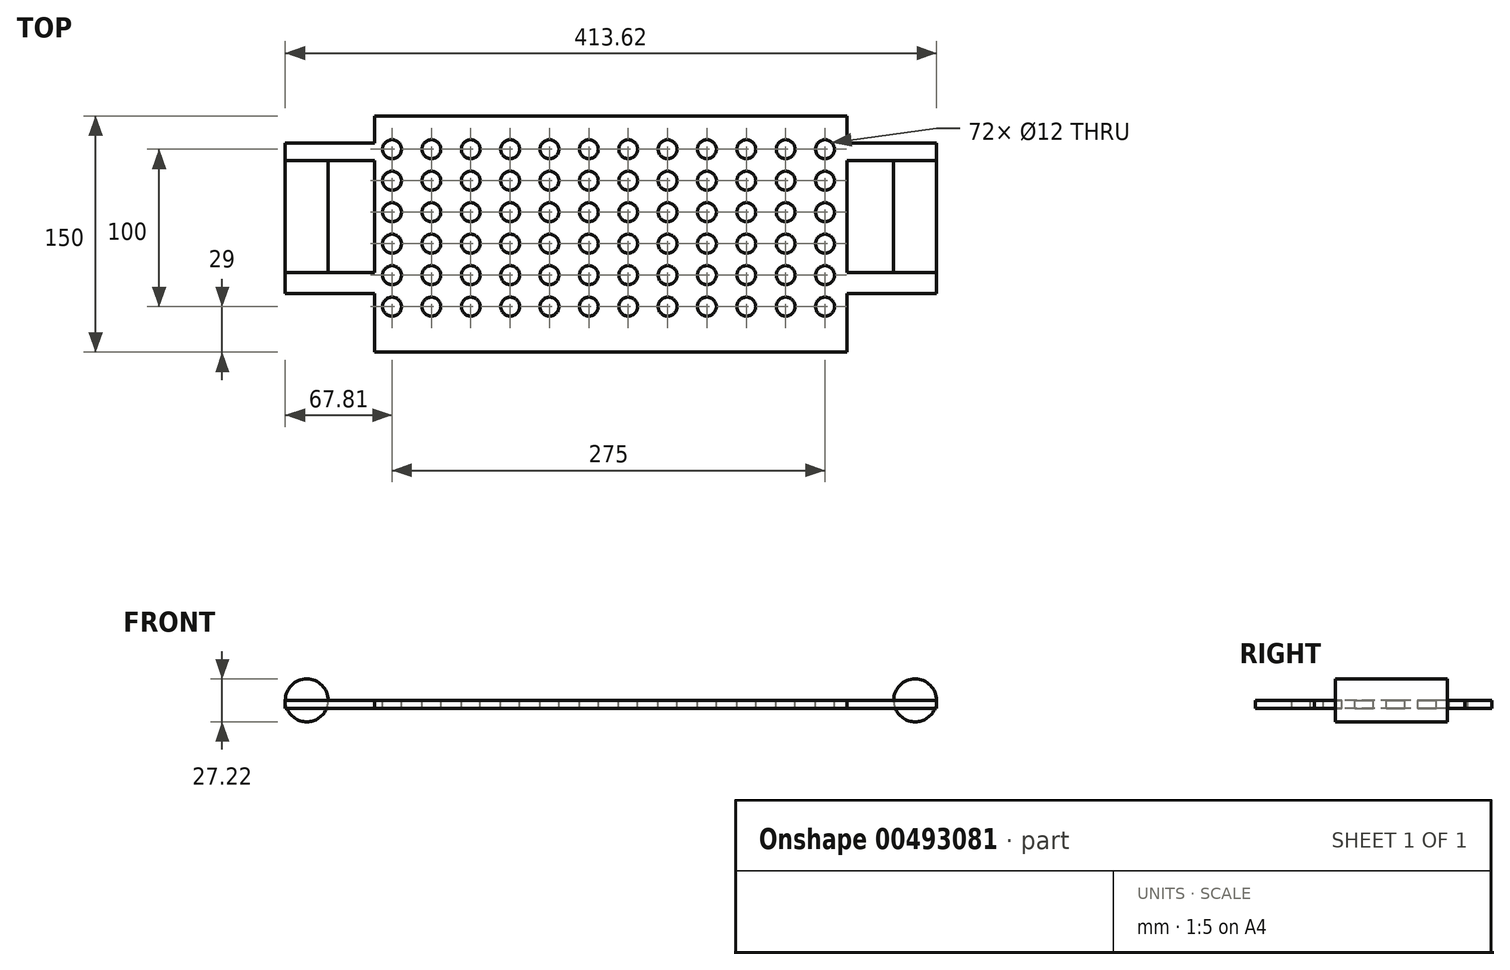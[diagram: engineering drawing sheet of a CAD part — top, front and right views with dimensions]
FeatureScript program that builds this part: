
annotation { "Feature Type Name" : "Feature", "Feature Type Description" : "" }
export const myFeature = defineFeature(function(context is Context, id is Id, definition is map)
    precondition{}
    {
        {
            var Q0;
            Q0=qCreatedBy(makeId("Top.planeOp"),FACE);
            var sketch = newSketch(context, id + "F0", { "sketchPlane" : qUnion([Q0])});
            skLineSegment(sketch, "E0.bottom", {"start": v(-150, 75) * mm, "end": v(150, 75) * mm});
            skLineSegment(sketch, "E0.top", {"start": v(-150, -75) * mm, "end": v(150, -75) * mm});
            skLineSegment(sketch, "E0.left", {"start": v(-150, 75) * mm, "end": v(-150, -75) * mm});
            skLineSegment(sketch, "E0.right", {"start": v(150, 75) * mm, "end": v(150, -75) * mm});
            skCircle(sketch, "E1", {"center": v(-139, 54) * mm, "radius": 6 * mm});
            skCircle(sketch, "E2.0.1.0", {"center": v(-139, 34) * mm, "radius": 6 * mm});
            skCircle(sketch, "E2.0.2.0", {"center": v(-139, 14) * mm, "radius": 6 * mm});
            skCircle(sketch, "E2.0.3.0", {"center": v(-139, -6) * mm, "radius": 6 * mm});
            skCircle(sketch, "E2.0.4.0", {"center": v(-139, -26) * mm, "radius": 6 * mm});
            skCircle(sketch, "E2.0.5.0", {"center": v(-139, -46) * mm, "radius": 6 * mm});
            skCircle(sketch, "E2.1.0.0", {"center": v(-114, 54) * mm, "radius": 6 * mm});
            skCircle(sketch, "E2.1.1.0", {"center": v(-114, 34) * mm, "radius": 6 * mm});
            skCircle(sketch, "E2.1.2.0", {"center": v(-114, 14) * mm, "radius": 6 * mm});
            skCircle(sketch, "E2.1.3.0", {"center": v(-114, -6) * mm, "radius": 6 * mm});
            skCircle(sketch, "E2.1.4.0", {"center": v(-114, -26) * mm, "radius": 6 * mm});
            skCircle(sketch, "E2.1.5.0", {"center": v(-114, -46) * mm, "radius": 6 * mm});
            skCircle(sketch, "E2.2.0.0", {"center": v(-89, 54) * mm, "radius": 6 * mm});
            skCircle(sketch, "E2.2.1.0", {"center": v(-89, 34) * mm, "radius": 6 * mm});
            skCircle(sketch, "E2.2.2.0", {"center": v(-89, 14) * mm, "radius": 6 * mm});
            skCircle(sketch, "E2.2.3.0", {"center": v(-89, -6) * mm, "radius": 6 * mm});
            skCircle(sketch, "E2.2.4.0", {"center": v(-89, -26) * mm, "radius": 6 * mm});
            skCircle(sketch, "E2.2.5.0", {"center": v(-89, -46) * mm, "radius": 6 * mm});
            skCircle(sketch, "E2.3.0.0", {"center": v(-64, 54) * mm, "radius": 6 * mm});
            skCircle(sketch, "E2.3.1.0", {"center": v(-64, 34) * mm, "radius": 6 * mm});
            skCircle(sketch, "E2.3.2.0", {"center": v(-64, 14) * mm, "radius": 6 * mm});
            skCircle(sketch, "E2.3.3.0", {"center": v(-64, -6) * mm, "radius": 6 * mm});
            skCircle(sketch, "E2.3.4.0", {"center": v(-64, -26) * mm, "radius": 6 * mm});
            skCircle(sketch, "E2.3.5.0", {"center": v(-64, -46) * mm, "radius": 6 * mm});
            skCircle(sketch, "E2.4.0.0", {"center": v(-39, 54) * mm, "radius": 6 * mm});
            skCircle(sketch, "E2.4.1.0", {"center": v(-39, 34) * mm, "radius": 6 * mm});
            skCircle(sketch, "E2.4.2.0", {"center": v(-39, 14) * mm, "radius": 6 * mm});
            skCircle(sketch, "E2.4.3.0", {"center": v(-39, -6) * mm, "radius": 6 * mm});
            skCircle(sketch, "E2.4.4.0", {"center": v(-39, -26) * mm, "radius": 6 * mm});
            skCircle(sketch, "E2.4.5.0", {"center": v(-39, -46) * mm, "radius": 6 * mm});
            skCircle(sketch, "E2.5.0.0", {"center": v(-14, 54) * mm, "radius": 6 * mm});
            skCircle(sketch, "E2.5.1.0", {"center": v(-14, 34) * mm, "radius": 6 * mm});
            skCircle(sketch, "E2.5.2.0", {"center": v(-14, 14) * mm, "radius": 6 * mm});
            skCircle(sketch, "E2.5.3.0", {"center": v(-14, -6) * mm, "radius": 6 * mm});
            skCircle(sketch, "E2.5.4.0", {"center": v(-14, -26) * mm, "radius": 6 * mm});
            skCircle(sketch, "E2.5.5.0", {"center": v(-14, -46) * mm, "radius": 6 * mm});
            skCircle(sketch, "E2.6.0.0", {"center": v(11, 54) * mm, "radius": 6 * mm});
            skCircle(sketch, "E2.6.1.0", {"center": v(11, 34) * mm, "radius": 6 * mm});
            skCircle(sketch, "E2.6.2.0", {"center": v(11, 14) * mm, "radius": 6 * mm});
            skCircle(sketch, "E2.6.3.0", {"center": v(11, -6) * mm, "radius": 6 * mm});
            skCircle(sketch, "E2.6.4.0", {"center": v(11, -26) * mm, "radius": 6 * mm});
            skCircle(sketch, "E2.6.5.0", {"center": v(11, -46) * mm, "radius": 6 * mm});
            skCircle(sketch, "E2.7.0.0", {"center": v(36, 54) * mm, "radius": 6 * mm});
            skCircle(sketch, "E2.7.1.0", {"center": v(36, 34) * mm, "radius": 6 * mm});
            skCircle(sketch, "E2.7.2.0", {"center": v(36, 14) * mm, "radius": 6 * mm});
            skCircle(sketch, "E2.7.3.0", {"center": v(36, -6) * mm, "radius": 6 * mm});
            skCircle(sketch, "E2.7.4.0", {"center": v(36, -26) * mm, "radius": 6 * mm});
            skCircle(sketch, "E2.7.5.0", {"center": v(36, -46) * mm, "radius": 6 * mm});
            skCircle(sketch, "E2.8.0.0", {"center": v(61, 54) * mm, "radius": 6 * mm});
            skCircle(sketch, "E2.8.1.0", {"center": v(61, 34) * mm, "radius": 6 * mm});
            skCircle(sketch, "E2.8.2.0", {"center": v(61, 14) * mm, "radius": 6 * mm});
            skCircle(sketch, "E2.8.3.0", {"center": v(61, -6) * mm, "radius": 6 * mm});
            skCircle(sketch, "E2.8.4.0", {"center": v(61, -26) * mm, "radius": 6 * mm});
            skCircle(sketch, "E2.8.5.0", {"center": v(61, -46) * mm, "radius": 6 * mm});
            skCircle(sketch, "E2.9.0.0", {"center": v(86, 54) * mm, "radius": 6 * mm});
            skCircle(sketch, "E2.9.1.0", {"center": v(86, 34) * mm, "radius": 6 * mm});
            skCircle(sketch, "E2.9.2.0", {"center": v(86, 14) * mm, "radius": 6 * mm});
            skCircle(sketch, "E2.9.3.0", {"center": v(86, -6) * mm, "radius": 6 * mm});
            skCircle(sketch, "E2.9.4.0", {"center": v(86, -26) * mm, "radius": 6 * mm});
            skCircle(sketch, "E2.9.5.0", {"center": v(86, -46) * mm, "radius": 6 * mm});
            skCircle(sketch, "E2.10.0.0", {"center": v(111, 54) * mm, "radius": 6 * mm});
            skCircle(sketch, "E2.10.1.0", {"center": v(111, 34) * mm, "radius": 6 * mm});
            skCircle(sketch, "E2.10.2.0", {"center": v(111, 14) * mm, "radius": 6 * mm});
            skCircle(sketch, "E2.10.3.0", {"center": v(111, -6) * mm, "radius": 6 * mm});
            skCircle(sketch, "E2.10.4.0", {"center": v(111, -26) * mm, "radius": 6 * mm});
            skCircle(sketch, "E2.10.5.0", {"center": v(111, -46) * mm, "radius": 6 * mm});
            skCircle(sketch, "E2.11.0.0", {"center": v(136, 54) * mm, "radius": 6 * mm});
            skCircle(sketch, "E2.11.1.0", {"center": v(136, 34) * mm, "radius": 6 * mm});
            skCircle(sketch, "E2.11.2.0", {"center": v(136, 14) * mm, "radius": 6 * mm});
            skCircle(sketch, "E2.11.3.0", {"center": v(136, -6) * mm, "radius": 6 * mm});
            skCircle(sketch, "E2.11.4.0", {"center": v(136, -26) * mm, "radius": 6 * mm});
            skCircle(sketch, "E2.11.5.0", {"center": v(136, -46) * mm, "radius": 6 * mm});
            skLineSegment(sketch, "E2.direction1", {"start": v(-139, 54) * mm, "end": v(-114, 54) * mm, "construction": true});
            skLineSegment(sketch, "E2.direction2", {"start": v(-139, 54) * mm, "end": v(-139, 34) * mm, "construction": true});
            skLineSegment(sketch, "E3", {"start": v(150, 46.77) * mm, "end": v(193.2, 46.77) * mm});
            skLineSegment(sketch, "E4", {"start": v(193.2, 46.77) * mm, "end": v(193.2, -24.3) * mm});
            skLineSegment(sketch, "E5", {"start": v(193.2, -24.3) * mm, "end": v(150, -24.3) * mm});
            skLineSegment(sketch, "E6", {"start": v(150, -37.55) * mm, "end": v(206.81, -37.55) * mm});
            skLineSegment(sketch, "E7", {"start": v(206.81, -37.55) * mm, "end": v(206.81, 57.84) * mm});
            skLineSegment(sketch, "E8", {"start": v(206.81, 57.84) * mm, "end": v(150, 57.84) * mm});
            skLineSegment(sketch, "E9", {"start": v(193.2, -24.3) * mm, "end": v(206.81, -24.3) * mm});
            skLineSegment(sketch, "E10", {"start": v(193.2, 46.77) * mm, "end": v(206.81, 46.77) * mm});
            skLineSegment(sketch, "E11.MirrorCS", {"start": v(-206.81, 57.84) * mm, "end": v(-150, 57.84) * mm});
            skLineSegment(sketch, "E12.MirrorCS", {"start": v(-150, 46.77) * mm, "end": v(-193.2, 46.77) * mm});
            skLineSegment(sketch, "E13.MirrorCS", {"start": v(-193.2, 46.77) * mm, "end": v(-206.81, 46.77) * mm});
            skLineSegment(sketch, "E14.MirrorCS", {"start": v(-193.2, 46.77) * mm, "end": v(-193.2, -24.3) * mm});
            skLineSegment(sketch, "E15.MirrorCS", {"start": v(-206.81, -37.55) * mm, "end": v(-206.81, 57.84) * mm});
            skLineSegment(sketch, "E16.MirrorCS", {"start": v(-193.2, -24.3) * mm, "end": v(-150, -24.3) * mm});
            skLineSegment(sketch, "E17.MirrorCS", {"start": v(-193.2, -24.3) * mm, "end": v(-206.81, -24.3) * mm});
            skLineSegment(sketch, "E18.MirrorCS", {"start": v(-150, -37.55) * mm, "end": v(-206.81, -37.55) * mm});
            skSolve(sketch);
        }
        {
            var Q0;
            Q0=makeQuery(id+"F0.imprint","IMPRINT",FACE,{"disambiguationData":[TD([[makeQuery(id+"F0.imprint","IMPRINT",EDGE,{"derivedFrom":sQuery(id+"F0.wireOp",EDGE,"E0.bottom")}),-1.0]])]});
            var Q1;
            {var subQ3=sQuery(id+"F0.wireOp",EDGE,"E3");Q1=makeQuery(id+"F0.imprint","IMPRINT",FACE,{"disambiguationData":[TD([[makeQuery(id+"F0.imprint","IMPRINT",EDGE,{"derivedFrom":subQ3}),1.0]])]});}
            var Q2;
            {var subQ3=sQuery(id+"F0.wireOp",EDGE,"E5");Q2=makeQuery(id+"F0.imprint","IMPRINT",FACE,{"disambiguationData":[TD([[makeQuery(id+"F0.imprint","IMPRINT",EDGE,{"derivedFrom":subQ3}),1.0]])]});}
            var Q3;
            {var subQ2=sQuery(id+"F0.wireOp",EDGE,"E11.MirrorCS");Q3=makeQuery(id+"F0.imprint","IMPRINT",FACE,{"disambiguationData":[TD([[makeQuery(id+"F0.imprint","IMPRINT",EDGE,{"derivedFrom":subQ2}),-1.0]])]});}
            var Q4;
            {var subQ1=sQuery(id+"F0.wireOp",EDGE,"E16.MirrorCS");Q4=makeQuery(id+"F0.imprint","IMPRINT",FACE,{"disambiguationData":[TD([[makeQuery(id+"F0.imprint","IMPRINT",EDGE,{"derivedFrom":subQ1}),-1.0]])]});}
            extrude(context, id + "F1", {"entities" : qUnion([Q0, Q1, Q2, Q3, Q4]), "oppositeDirection" : true, "depth" : 5 * mm});
        }
        {
            var Q0;
            {var subQ0=sQuery(id+"F0.wireOp",EDGE,"E13.MirrorCS");Q0=makeQuery(id+"F0.imprint","IMPRINT",FACE,{"disambiguationData":[TD([[makeQuery(id+"F0.imprint","IMPRINT",EDGE,{"derivedFrom":subQ0}),1.0]])]});}
            var Q1;
            Q1=sQuery(id+"F0.wireOp",EDGE,"E14.MirrorCS");
            revolve(context, id + "F2", {"entities" : qUnion([Q0]), "axis" : qUnion([Q1]), "revolveType" : RevolveType.FULL});
        }
        {
            var Q0;
            Q0=makeQuery(id+"F2.opRevolve","SWEPT_BODY",BODY,{"disambiguationData":[OSD([sQuery(id+"F0.wireOp",EDGE,"E13.MirrorCS"),sQuery(id+"F0.wireOp",EDGE,"E14.MirrorCS"),sQuery(id+"F0.wireOp",EDGE,"E15.MirrorCS"),sQuery(id+"F0.wireOp",EDGE,"E17.MirrorCS")])]});
            var Q1;
            Q1=qCreatedBy(makeId("Right.planeOp"),FACE);
            mirror(context, id + "F3", {"entities" : qUnion([Q0]), "mirrorPlane" : qUnion([Q1])});
        }
    });
